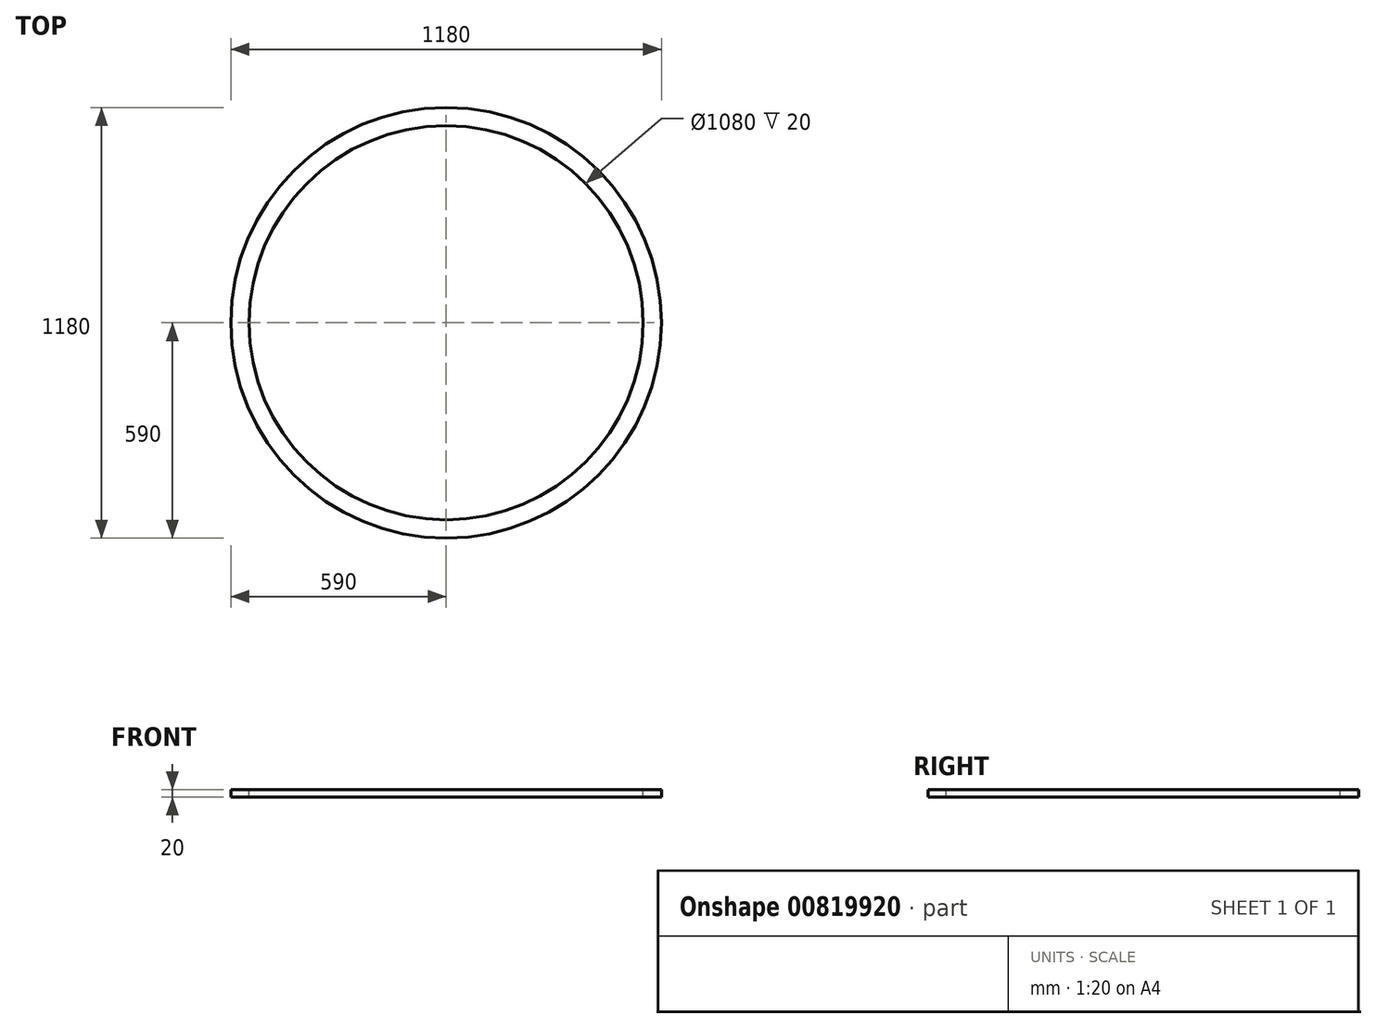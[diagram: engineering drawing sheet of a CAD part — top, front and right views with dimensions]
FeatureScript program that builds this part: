
annotation { "Feature Type Name" : "Feature", "Feature Type Description" : "" }
export const myFeature = defineFeature(function(context is Context, id is Id, definition is map)
    precondition{}
    {
        {
            var Q0;
            Q0=qCreatedBy(makeId("Top.planeOp"),FACE);
            var sketch = newSketch(context, id + "F0", { "sketchPlane" : qUnion([Q0])});
            skCircle(sketch, "E0", {"center": v(0, 0) * mm, "radius": 590 * mm});
            skCircle(sketch, "E1.0", {"center": v(0, 0) * mm, "radius": 540 * mm});
            skSolve(sketch);
        }
        {
            var Q0;
            Q0=makeQuery(id+"F0.imprint","IMPRINT",FACE,{"disambiguationData":[TD([[makeQuery(id+"F0.imprint","IMPRINT",EDGE,{"derivedFrom":sQuery(id+"F0.wireOp",EDGE,"E0")}),1.0]])]});
            extrude(context, id + "F1", {"entities" : qUnion([Q0]), "oppositeDirection" : true, "depth" : 20 * mm, "offsetDistance" : 25 * mm});
        }
    });
